# Revit family: Graypants_Roest_Sconce30_R21_0925
name_source: partatom
category: Lighting Fixtures
units: mm (PartAtom-declared; Revit-internal decimal feet)

## family parameters
Cut with Voids When Loaded = No
Host = Face
Light Source = Yes
Part Type = Normal
Room Calculation Point = No
Round Connector Dimension = Use Diameter
Shared = No

## types (1)
- Graypants_Roest_Sconce30
    Color Filter = 16777215
    Default Elevation = 4' - 0"
    Dimming Lamp Color Temperature Shift = <None>
    Emit from Line Length = 0' - 11 13/16"
    Graypants_Apparent_Load = GU10, Max 10W LED
 | Optional Integrated LED - 12W
    Graypants_Cord/Canopy_Finish_Options = Black
    Graypants_Cord_Material_Finish = _Graypants_Black_Finish
    Graypants_Description = The Roest collection bends the norm with its unpretentious simplicity, in which the design has met no equal. Nature’s reaction between 
iron, oxygen, water and time. Designed by VanJoost and hand-made in Holland, Roest presents natural colors in unusual settings.
    Graypants_Dimming = GU10 - Depending on lamp | 
Optional Integrated LED - 0-10v or Triac/ELV
    Graypants_Initial_Color_Temperature = GU10 - 2700K Recommended / Dependant on Lamp | 
Integrated LED - 2700K
    Graypants_Initial_Intensity = GU10 - Dependant on Lamp | 
Optional Integrated LED - NA
    Graypants_Manufacturer = Graypants
    Graypants_Model = Sconce30
    Graypants_Product_Visible = Yes
    Graypants_SKU = Sconce30 Rust - GP2052-N
 | Sconce30 Zinc - GP2053-AZ
 | Sconce30 Carbon - GP2054-C
    Graypants_Shade_Finish_Options = Rust
 | Zinc
 | Carbon
    Graypants_Spec_Sheet = https://www.dropbox.com
    Graypants_URL = www.graypants.com
    Graypants_Voltage = GU10 - 120V | 
Optional Integrated LED - 120-277V
    Light Source Symbol Size = 0' - 2 3/8"

## geometry (parser evidence)
native form markers: Sweep x6
no freeform markers — native parametric forms only
